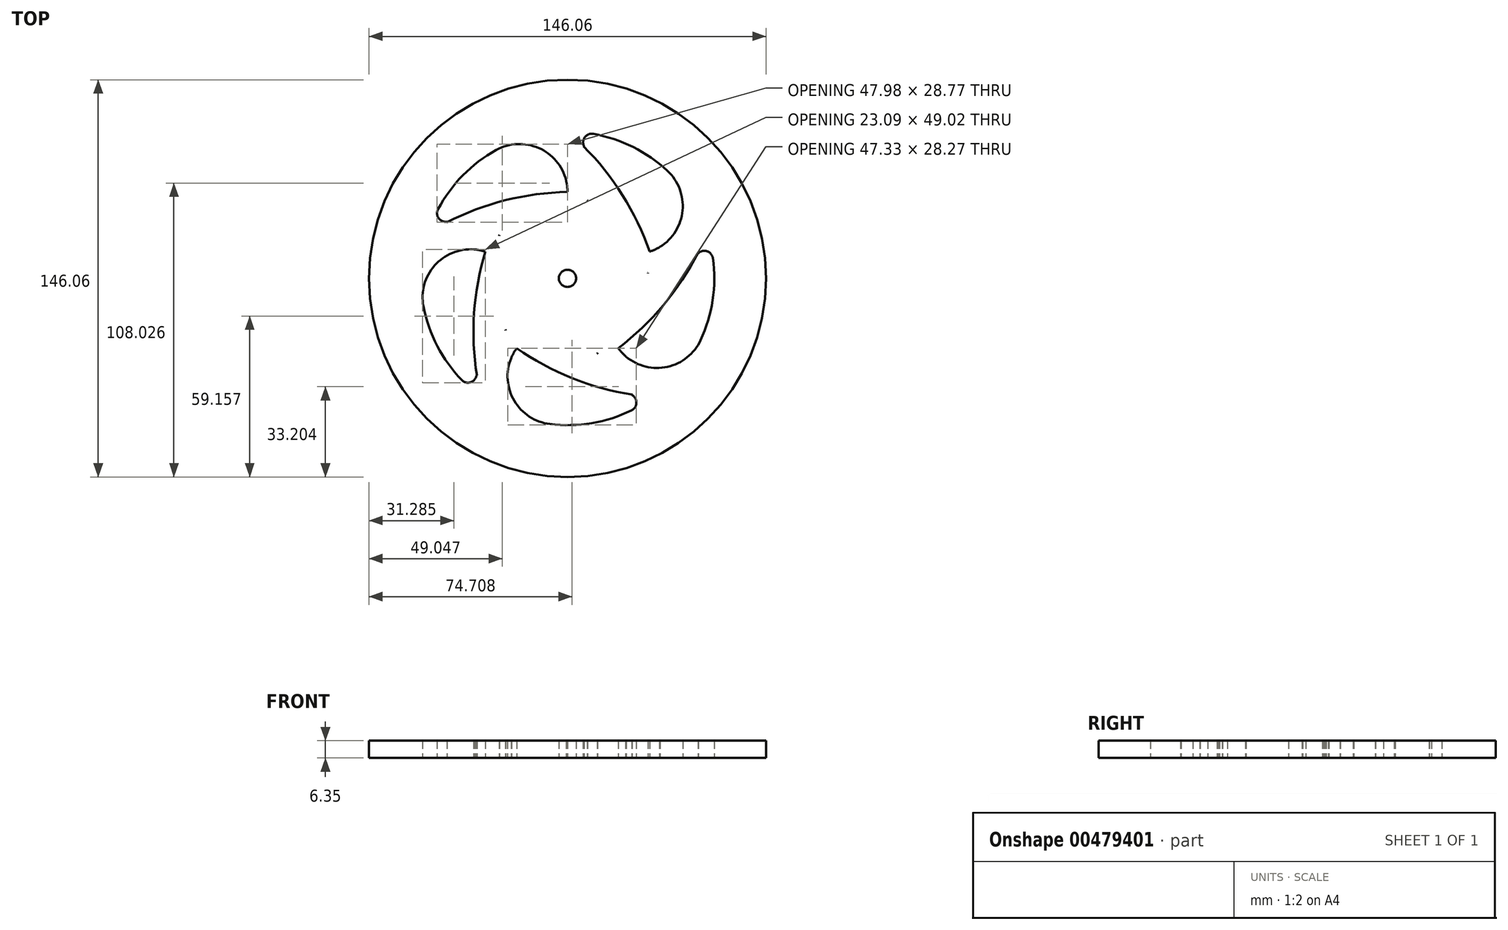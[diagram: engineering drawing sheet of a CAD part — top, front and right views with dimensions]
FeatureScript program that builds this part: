
annotation { "Feature Type Name" : "Feature", "Feature Type Description" : "" }
export const myFeature = defineFeature(function(context is Context, id is Id, definition is map)
    precondition{}
    {
        {
            var Q0;
            Q0=qCreatedBy(makeId("Top.planeOp"),FACE);
            var sketch = newSketch(context, id + "F0", { "sketchPlane" : qUnion([Q0]), "disableImprinting" : false});
            skCircle(sketch, "E0", {"center": v(0, 0) * mm, "radius": 73.03 * mm});
            skCircle(sketch, "E1", {"center": v(0, 0) * mm, "radius": 69.85 * mm});
            skLineSegment(sketch, "E2", {"start": v(-42.62, 55.34) * mm, "end": v(39.47, 57.63) * mm});
            skLineSegment(sketch, "E3", {"start": v(-42.62, 55.34) * mm, "end": v(-65.8, -23.44) * mm});
            skLineSegment(sketch, "E4", {"start": v(-65.8, -23.44) * mm, "end": v(1.96, -69.82) * mm});
            skLineSegment(sketch, "E5", {"start": v(1.96, -69.82) * mm, "end": v(67.01, -19.7) * mm});
            skLineSegment(sketch, "E6", {"start": v(67.01, -19.7) * mm, "end": v(39.47, 57.63) * mm});
            skCircle(sketch, "E7", {"center": v(1.96, -69.82) * mm, "radius": 101.6 * mm});
            skCircle(sketch, "E8", {"center": v(67.01, -19.7) * mm, "radius": 101.6 * mm});
            skCircle(sketch, "E9", {"center": v(39.47, 57.63) * mm, "radius": 101.6 * mm});
            skCircle(sketch, "E10", {"center": v(-42.62, 55.34) * mm, "radius": 101.6 * mm});
            skCircle(sketch, "E11", {"center": v(-65.8, -23.44) * mm, "radius": 101.6 * mm});
            skLineSegment(sketch, "E12", {"start": v(-232.09, 0) * mm, "end": v(227.68, 0) * mm});
            skCircle(sketch, "E13", {"center": v(0, 0) * mm, "radius": 53.97 * mm});
            skCircle(sketch, "E14.cCircle", {"center": v(0, 0) * mm, "radius": 36.32 * mm, "construction": true});
            skLineSegment(sketch, "E14.0", {"start": v(32.94, -15.31) * mm, "end": v(-4.38, -36.06) * mm});
            skLineSegment(sketch, "E14.1", {"start": v(-4.38, -36.06) * mm, "end": v(-35.65, -6.97) * mm});
            skLineSegment(sketch, "E14.2", {"start": v(-35.65, -6.97) * mm, "end": v(-17.65, 31.75) * mm});
            skLineSegment(sketch, "E14.3", {"start": v(-17.65, 31.75) * mm, "end": v(24.74, 26.6) * mm});
            skLineSegment(sketch, "E14.4", {"start": v(24.74, 26.6) * mm, "end": v(32.94, -15.31) * mm});
            skCircle(sketch, "E15", {"center": v(24.74, 26.6) * mm, "radius": 17.65 * mm});
            skCircle(sketch, "E16", {"center": v(-17.65, 31.75) * mm, "radius": 17.65 * mm});
            skCircle(sketch, "E17", {"center": v(-35.65, -6.97) * mm, "radius": 17.65 * mm});
            skCircle(sketch, "E18", {"center": v(-4.38, -36.06) * mm, "radius": 17.65 * mm});
            skCircle(sketch, "E19", {"center": v(32.94, -15.31) * mm, "radius": 17.65 * mm});
            skCircle(sketch, "E20.cCircle", {"center": v(0, 0) * mm, "radius": 50.8 * mm, "construction": true});
            skLineSegment(sketch, "E20.0", {"start": v(22.17, -45.7) * mm, "end": v(-36.62, -35.2) * mm});
            skLineSegment(sketch, "E20.1", {"start": v(-36.62, -35.2) * mm, "end": v(-44.8, 23.95) * mm});
            skLineSegment(sketch, "E20.2", {"start": v(-44.8, 23.95) * mm, "end": v(8.93, 50) * mm});
            skLineSegment(sketch, "E20.3", {"start": v(8.93, 50) * mm, "end": v(50.32, 6.96) * mm});
            skLineSegment(sketch, "E20.4", {"start": v(50.32, 6.96) * mm, "end": v(22.17, -45.7) * mm});
            skCircle(sketch, "E21", {"center": v(50.32, 6.96) * mm, "radius": 3.18 * mm});
            skCircle(sketch, "E22", {"center": v(8.93, 50) * mm, "radius": 3.18 * mm});
            skCircle(sketch, "E23", {"center": v(-44.8, 23.95) * mm, "radius": 3.18 * mm});
            skCircle(sketch, "E24", {"center": v(-36.62, -35.2) * mm, "radius": 3.18 * mm});
            skCircle(sketch, "E25", {"center": v(22.17, -45.7) * mm, "radius": 3.18 * mm});
            skCircle(sketch, "E26.cCircle", {"center": v(0, 0) * mm, "radius": 35.27 * mm, "construction": true});
            skLineSegment(sketch, "E26.0", {"start": v(23.5, -26.3) * mm, "end": v(-17.75, -30.48) * mm});
            skLineSegment(sketch, "E26.1", {"start": v(-17.75, -30.48) * mm, "end": v(-34.47, 7.46) * mm});
            skLineSegment(sketch, "E26.2", {"start": v(-34.47, 7.46) * mm, "end": v(-3.56, 35.09) * mm});
            skLineSegment(sketch, "E26.3", {"start": v(-3.56, 35.09) * mm, "end": v(32.27, 14.22) * mm});
            skLineSegment(sketch, "E26.4", {"start": v(32.27, 14.22) * mm, "end": v(23.5, -26.3) * mm});
            skCircle(sketch, "E27", {"center": v(32.27, 14.22) * mm, "radius": 3.18 * mm});
            skCircle(sketch, "E28", {"center": v(-3.56, 35.09) * mm, "radius": 3.18 * mm});
            skCircle(sketch, "E29", {"center": v(-34.47, 7.46) * mm, "radius": 3.18 * mm});
            skCircle(sketch, "E30", {"center": v(-17.75, -30.48) * mm, "radius": 3.18 * mm});
            skCircle(sketch, "E31", {"center": v(23.5, -26.3) * mm, "radius": 3.18 * mm});
            skCircle(sketch, "E32", {"center": v(0, 0) * mm, "radius": 3.18 * mm});
            skSolve(sketch);
        }
        {
            var Q0;
            {var subQ1=sQuery(id+"F0.wireOp",EDGE,"E0");var subQ6=sQuery(id+"F0.wireOp",EDGE,"E12");var subQ8=makeQuery(id+"F0.imprint","INTERSECT",VERTEX,{"disambiguationData":[OD(0.0)],"derivedFrom":[subQ1,subQ6]});Q0=makeQuery(id+"F0.imprint","IMPRINT",FACE,{"disambiguationData":[TD([[makeQuery(id+"F0.imprint","IMPRINT",EDGE,{"disambiguationData":[TD([[subQ8,1.0]])],"derivedFrom":subQ1}),1.0]])]});}
            var Q1;
            {var subQ0=sQuery(id+"F0.wireOp",EDGE,"E11");var subQ1=sQuery(id+"F0.wireOp",EDGE,"E0");var subQ2=makeQuery(id+"F0.imprint","INTERSECT",VERTEX,{"disambiguationData":[OD(1.0)],"derivedFrom":[subQ1,subQ0]});Q1=makeQuery(id+"F0.imprint","IMPRINT",FACE,{"disambiguationData":[TD([[makeQuery(id+"F0.imprint","IMPRINT",EDGE,{"disambiguationData":[TD([[subQ2,-1.0]])],"derivedFrom":subQ1}),1.0]])]});}
            var Q2;
            {var subQ0=sQuery(id+"F0.wireOp",EDGE,"E7");var subQ1=sQuery(id+"F0.wireOp",EDGE,"E0");var subQ2=makeQuery(id+"F0.imprint","INTERSECT",VERTEX,{"disambiguationData":[OD(0.0)],"derivedFrom":[subQ1,subQ0]});Q2=makeQuery(id+"F0.imprint","IMPRINT",FACE,{"disambiguationData":[TD([[makeQuery(id+"F0.imprint","IMPRINT",EDGE,{"disambiguationData":[TD([[subQ2,-1.0]])],"derivedFrom":subQ1}),1.0]])]});}
            var Q3;
            {var subQ0=sQuery(id+"F0.wireOp",EDGE,"E7");var subQ1=sQuery(id+"F0.wireOp",EDGE,"E0");var subQ2=makeQuery(id+"F0.imprint","INTERSECT",VERTEX,{"disambiguationData":[OD(0.0)],"derivedFrom":[subQ1,subQ0]});Q3=makeQuery(id+"F0.imprint","IMPRINT",FACE,{"disambiguationData":[TD([[makeQuery(id+"F0.imprint","IMPRINT",EDGE,{"disambiguationData":[TD([[subQ2,1.0]])],"derivedFrom":subQ1}),1.0]])]});}
            var Q4;
            {var subQ0=sQuery(id+"F0.wireOp",EDGE,"E8");var subQ1=sQuery(id+"F0.wireOp",EDGE,"E0");var subQ2=makeQuery(id+"F0.imprint","INTERSECT",VERTEX,{"disambiguationData":[OD(1.0)],"derivedFrom":[subQ1,subQ0]});Q4=makeQuery(id+"F0.imprint","IMPRINT",FACE,{"disambiguationData":[TD([[makeQuery(id+"F0.imprint","IMPRINT",EDGE,{"disambiguationData":[TD([[subQ2,-1.0]])],"derivedFrom":subQ1}),1.0]])]});}
            var Q5;
            {var subQ0=sQuery(id+"F0.wireOp",EDGE,"E10");var subQ1=sQuery(id+"F0.wireOp",EDGE,"E0");var subQ2=makeQuery(id+"F0.imprint","INTERSECT",VERTEX,{"disambiguationData":[OD(1.0)],"derivedFrom":[subQ1,subQ0]});Q5=makeQuery(id+"F0.imprint","IMPRINT",FACE,{"disambiguationData":[TD([[makeQuery(id+"F0.imprint","IMPRINT",EDGE,{"disambiguationData":[TD([[subQ2,-1.0]])],"derivedFrom":subQ1}),1.0]])]});}
            var Q6;
            {var subQ0=sQuery(id+"F0.wireOp",EDGE,"E7");var subQ1=sQuery(id+"F0.wireOp",EDGE,"E0");var subQ2=makeQuery(id+"F0.imprint","INTERSECT",VERTEX,{"disambiguationData":[OD(1.0)],"derivedFrom":[subQ1,subQ0]});Q6=makeQuery(id+"F0.imprint","IMPRINT",FACE,{"disambiguationData":[TD([[makeQuery(id+"F0.imprint","IMPRINT",EDGE,{"disambiguationData":[TD([[subQ2,-1.0]])],"derivedFrom":subQ1}),1.0]])]});}
            var Q7;
            {var subQ5=sQuery(id+"F0.wireOp",EDGE,"E9");var subQ6=sQuery(id+"F0.wireOp",EDGE,"E0");var subQ7=makeQuery(id+"F0.imprint","INTERSECT",VERTEX,{"disambiguationData":[OD(0.0)],"derivedFrom":[subQ6,subQ5]});Q7=makeQuery(id+"F0.imprint","IMPRINT",FACE,{"disambiguationData":[TD([[makeQuery(id+"F0.imprint","IMPRINT",EDGE,{"disambiguationData":[TD([[subQ7,-1.0]])],"derivedFrom":subQ6}),1.0]])]});}
            var Q8;
            {var subQ4=sQuery(id+"F0.wireOp",EDGE,"E11");var subQ6=sQuery(id+"F0.wireOp",EDGE,"E0");var subQ8=makeQuery(id+"F0.imprint","INTERSECT",VERTEX,{"disambiguationData":[OD(0.0)],"derivedFrom":[subQ6,subQ4]});Q8=makeQuery(id+"F0.imprint","IMPRINT",FACE,{"disambiguationData":[TD([[makeQuery(id+"F0.imprint","IMPRINT",EDGE,{"disambiguationData":[TD([[subQ8,-1.0]])],"derivedFrom":subQ6}),1.0]])]});}
            var Q9;
            {var subQ0=sQuery(id+"F0.wireOp",EDGE,"E8");var subQ1=sQuery(id+"F0.wireOp",EDGE,"E0");var subQ2=makeQuery(id+"F0.imprint","INTERSECT",VERTEX,{"disambiguationData":[OD(0.0)],"derivedFrom":[subQ1,subQ0]});Q9=makeQuery(id+"F0.imprint","IMPRINT",FACE,{"disambiguationData":[TD([[makeQuery(id+"F0.imprint","IMPRINT",EDGE,{"disambiguationData":[TD([[subQ2,-1.0]])],"derivedFrom":subQ1}),1.0]])]});}
            var Q10;
            {var subQ4=sQuery(id+"F0.wireOp",EDGE,"E10");var subQ6=sQuery(id+"F0.wireOp",EDGE,"E0");var subQ8=makeQuery(id+"F0.imprint","INTERSECT",VERTEX,{"disambiguationData":[OD(0.0)],"derivedFrom":[subQ6,subQ4]});Q10=makeQuery(id+"F0.imprint","IMPRINT",FACE,{"disambiguationData":[TD([[makeQuery(id+"F0.imprint","IMPRINT",EDGE,{"disambiguationData":[TD([[subQ8,-1.0]])],"derivedFrom":subQ6}),1.0]])]});}
            var Q11;
            {var subQ1=sQuery(id+"F0.wireOp",EDGE,"E1");var subQ3=sQuery(id+"F0.wireOp",EDGE,"E10");var subQ4=makeQuery(id+"F0.imprint","INTERSECT",VERTEX,{"disambiguationData":[OD(0.0)],"derivedFrom":[subQ1,subQ3]});Q11=makeQuery(id+"F0.imprint","IMPRINT",FACE,{"disambiguationData":[TD([[makeQuery(id+"F0.imprint","IMPRINT",EDGE,{"disambiguationData":[TD([[subQ4,1.0]])],"derivedFrom":subQ3}),1.0]])]});}
            var Q12;
            {var subQ0=sQuery(id+"F0.wireOp",EDGE,"E7");var subQ1=sQuery(id+"F0.wireOp",EDGE,"E1");var subQ2=makeQuery(id+"F0.imprint","INTERSECT",VERTEX,{"disambiguationData":[OD(0.0)],"derivedFrom":[subQ1,subQ0]});Q12=makeQuery(id+"F0.imprint","IMPRINT",FACE,{"disambiguationData":[TD([[makeQuery(id+"F0.imprint","IMPRINT",EDGE,{"disambiguationData":[TD([[subQ2,-1.0]])],"derivedFrom":subQ1}),1.0]])]});}
            var Q13;
            {var subQ0=sQuery(id+"F0.wireOp",EDGE,"E7");var subQ1=sQuery(id+"F0.wireOp",EDGE,"E1");var subQ2=makeQuery(id+"F0.imprint","INTERSECT",VERTEX,{"disambiguationData":[OD(0.0)],"derivedFrom":[subQ1,subQ0]});Q13=makeQuery(id+"F0.imprint","IMPRINT",FACE,{"disambiguationData":[TD([[makeQuery(id+"F0.imprint","IMPRINT",EDGE,{"disambiguationData":[TD([[subQ2,1.0]])],"derivedFrom":subQ1}),1.0]])]});}
            var Q14;
            {var subQ1=sQuery(id+"F0.wireOp",EDGE,"E1");var subQ3=sQuery(id+"F0.wireOp",EDGE,"E9");var subQ4=makeQuery(id+"F0.imprint","INTERSECT",VERTEX,{"disambiguationData":[OD(1.0)],"derivedFrom":[subQ1,subQ3]});Q14=makeQuery(id+"F0.imprint","IMPRINT",FACE,{"disambiguationData":[TD([[makeQuery(id+"F0.imprint","IMPRINT",EDGE,{"disambiguationData":[TD([[subQ4,1.0]])],"derivedFrom":subQ3}),1.0]])]});}
            var Q15;
            {var subQ0=sQuery(id+"F0.wireOp",EDGE,"E11");var subQ1=sQuery(id+"F0.wireOp",EDGE,"E1");var subQ2=makeQuery(id+"F0.imprint","INTERSECT",VERTEX,{"disambiguationData":[OD(1.0)],"derivedFrom":[subQ1,subQ0]});Q15=makeQuery(id+"F0.imprint","IMPRINT",FACE,{"disambiguationData":[TD([[makeQuery(id+"F0.imprint","IMPRINT",EDGE,{"disambiguationData":[TD([[subQ2,-1.0]])],"derivedFrom":subQ1}),1.0]])]});}
            var Q16;
            {var subQ1=sQuery(id+"F0.wireOp",EDGE,"E1");var subQ3=sQuery(id+"F0.wireOp",EDGE,"E11");var subQ4=makeQuery(id+"F0.imprint","INTERSECT",VERTEX,{"disambiguationData":[OD(1.0)],"derivedFrom":[subQ1,subQ3]});Q16=makeQuery(id+"F0.imprint","IMPRINT",FACE,{"disambiguationData":[TD([[makeQuery(id+"F0.imprint","IMPRINT",EDGE,{"disambiguationData":[TD([[subQ4,-1.0]])],"derivedFrom":subQ3}),1.0]])]});}
            var Q17;
            {var subQ0=sQuery(id+"F0.wireOp",EDGE,"E11");var subQ1=sQuery(id+"F0.wireOp",EDGE,"E5");var subQ2=makeQuery(id+"F0.imprint","INTERSECT",VERTEX,{"derivedFrom":[subQ1,subQ0]});Q17=makeQuery(id+"F0.imprint","IMPRINT",FACE,{"disambiguationData":[TD([[makeQuery(id+"F0.imprint","IMPRINT",EDGE,{"disambiguationData":[TD([[subQ2,-1.0]])],"derivedFrom":subQ1}),1.0]])]});}
            var Q18;
            {var subQ1=sQuery(id+"F0.wireOp",EDGE,"E1");var subQ3=sQuery(id+"F0.wireOp",EDGE,"E8");var subQ4=makeQuery(id+"F0.imprint","INTERSECT",VERTEX,{"disambiguationData":[OD(1.0)],"derivedFrom":[subQ1,subQ3]});Q18=makeQuery(id+"F0.imprint","IMPRINT",FACE,{"disambiguationData":[TD([[makeQuery(id+"F0.imprint","IMPRINT",EDGE,{"disambiguationData":[TD([[subQ4,1.0]])],"derivedFrom":subQ3}),1.0]])]});}
            var Q19;
            {var subQ0=sQuery(id+"F0.wireOp",EDGE,"E10");var subQ1=sQuery(id+"F0.wireOp",EDGE,"E1");var subQ2=makeQuery(id+"F0.imprint","INTERSECT",VERTEX,{"disambiguationData":[OD(1.0)],"derivedFrom":[subQ1,subQ0]});Q19=makeQuery(id+"F0.imprint","IMPRINT",FACE,{"disambiguationData":[TD([[makeQuery(id+"F0.imprint","IMPRINT",EDGE,{"disambiguationData":[TD([[subQ2,-1.0]])],"derivedFrom":subQ1}),1.0]])]});}
            var Q20;
            {var subQ1=sQuery(id+"F0.wireOp",EDGE,"E1");var subQ3=sQuery(id+"F0.wireOp",EDGE,"E12");var subQ4=makeQuery(id+"F0.imprint","INTERSECT",VERTEX,{"disambiguationData":[OD(1.0)],"derivedFrom":[subQ1,subQ3]});Q20=makeQuery(id+"F0.imprint","IMPRINT",FACE,{"disambiguationData":[TD([[makeQuery(id+"F0.imprint","IMPRINT",EDGE,{"disambiguationData":[TD([[subQ4,-1.0]])],"derivedFrom":subQ3}),-1.0]])]});}
            var Q21;
            {var subQ0=sQuery(id+"F0.wireOp",EDGE,"E7");var subQ1=sQuery(id+"F0.wireOp",EDGE,"E1");var subQ2=makeQuery(id+"F0.imprint","INTERSECT",VERTEX,{"disambiguationData":[OD(1.0)],"derivedFrom":[subQ1,subQ0]});Q21=makeQuery(id+"F0.imprint","IMPRINT",FACE,{"disambiguationData":[TD([[makeQuery(id+"F0.imprint","IMPRINT",EDGE,{"disambiguationData":[TD([[subQ2,-1.0]])],"derivedFrom":subQ1}),-1.0]])]});}
            var Q22;
            {var subQ0=sQuery(id+"F0.wireOp",EDGE,"E12");var subQ1=sQuery(id+"F0.wireOp",EDGE,"E0");var subQ2=makeQuery(id+"F0.imprint","INTERSECT",VERTEX,{"disambiguationData":[OD(1.0)],"derivedFrom":[subQ1,subQ0]});Q22=makeQuery(id+"F0.imprint","IMPRINT",FACE,{"disambiguationData":[TD([[makeQuery(id+"F0.imprint","IMPRINT",EDGE,{"disambiguationData":[TD([[subQ2,-1.0]])],"derivedFrom":subQ1}),1.0]])]});}
            var Q23;
            {var subQ0=sQuery(id+"F0.wireOp",EDGE,"E9");var subQ1=sQuery(id+"F0.wireOp",EDGE,"E1");var subQ2=makeQuery(id+"F0.imprint","INTERSECT",VERTEX,{"disambiguationData":[OD(0.0)],"derivedFrom":[subQ1,subQ0]});Q23=makeQuery(id+"F0.imprint","IMPRINT",FACE,{"disambiguationData":[TD([[makeQuery(id+"F0.imprint","IMPRINT",EDGE,{"disambiguationData":[TD([[subQ2,-1.0]])],"derivedFrom":subQ1}),1.0]])]});}
            var Q24;
            {var subQ1=sQuery(id+"F0.wireOp",EDGE,"E1");var subQ3=sQuery(id+"F0.wireOp",EDGE,"E9");var subQ4=makeQuery(id+"F0.imprint","INTERSECT",VERTEX,{"disambiguationData":[OD(0.0)],"derivedFrom":[subQ1,subQ3]});Q24=makeQuery(id+"F0.imprint","IMPRINT",FACE,{"disambiguationData":[TD([[makeQuery(id+"F0.imprint","IMPRINT",EDGE,{"disambiguationData":[TD([[subQ4,-1.0]])],"derivedFrom":subQ3}),1.0]])]});}
            var Q25;
            {var subQ1=sQuery(id+"F0.wireOp",EDGE,"E1");var subQ3=sQuery(id+"F0.wireOp",EDGE,"E11");var subQ4=makeQuery(id+"F0.imprint","INTERSECT",VERTEX,{"disambiguationData":[OD(0.0)],"derivedFrom":[subQ1,subQ3]});Q25=makeQuery(id+"F0.imprint","IMPRINT",FACE,{"disambiguationData":[TD([[makeQuery(id+"F0.imprint","IMPRINT",EDGE,{"disambiguationData":[TD([[subQ4,1.0]])],"derivedFrom":subQ3}),1.0]])]});}
            var Q26;
            {var subQ1=sQuery(id+"F0.wireOp",EDGE,"E1");var subQ3=sQuery(id+"F0.wireOp",EDGE,"E8");var subQ4=makeQuery(id+"F0.imprint","INTERSECT",VERTEX,{"disambiguationData":[OD(0.0)],"derivedFrom":[subQ1,subQ3]});Q26=makeQuery(id+"F0.imprint","IMPRINT",FACE,{"disambiguationData":[TD([[makeQuery(id+"F0.imprint","IMPRINT",EDGE,{"disambiguationData":[TD([[subQ4,-1.0]])],"derivedFrom":subQ3}),1.0]])]});}
            var Q27;
            {var subQ0=sQuery(id+"F0.wireOp",EDGE,"E8");var subQ1=sQuery(id+"F0.wireOp",EDGE,"E1");var subQ2=makeQuery(id+"F0.imprint","INTERSECT",VERTEX,{"disambiguationData":[OD(0.0)],"derivedFrom":[subQ1,subQ0]});Q27=makeQuery(id+"F0.imprint","IMPRINT",FACE,{"disambiguationData":[TD([[makeQuery(id+"F0.imprint","IMPRINT",EDGE,{"disambiguationData":[TD([[subQ2,-1.0]])],"derivedFrom":subQ1}),1.0]])]});}
            var Q28;
            {var subQ3=sQuery(id+"F0.wireOp",EDGE,"E13");var subQ5=sQuery(id+"F0.wireOp",EDGE,"E7");var subQ6=makeQuery(id+"F0.imprint","INTERSECT",VERTEX,{"disambiguationData":[OD(1.0)],"derivedFrom":[subQ5,subQ3]});Q28=makeQuery(id+"F0.imprint","IMPRINT",FACE,{"disambiguationData":[TD([[makeQuery(id+"F0.imprint","IMPRINT",EDGE,{"disambiguationData":[TD([[subQ6,-1.0]])],"derivedFrom":subQ5}),-1.0]])]});}
            var Q29;
            {var subQ0=sQuery(id+"F0.wireOp",EDGE,"E11");var subQ1=sQuery(id+"F0.wireOp",EDGE,"E2");var subQ2=makeQuery(id+"F0.imprint","INTERSECT",VERTEX,{"derivedFrom":[subQ1,subQ0]});Q29=makeQuery(id+"F0.imprint","IMPRINT",FACE,{"disambiguationData":[TD([[makeQuery(id+"F0.imprint","IMPRINT",EDGE,{"disambiguationData":[TD([[subQ2,-1.0]])],"derivedFrom":subQ1}),-1.0]])]});}
            var Q30;
            {var subQ0=sQuery(id+"F0.wireOp",EDGE,"E11");var subQ1=sQuery(id+"F0.wireOp",EDGE,"E8");var subQ2=makeQuery(id+"F0.imprint","INTERSECT",VERTEX,{"disambiguationData":[OD(0.0)],"derivedFrom":[subQ1,subQ0]});Q30=makeQuery(id+"F0.imprint","IMPRINT",FACE,{"disambiguationData":[TD([[makeQuery(id+"F0.imprint","IMPRINT",EDGE,{"disambiguationData":[TD([[subQ2,-1.0]])],"derivedFrom":subQ1}),1.0]])]});}
            var Q31;
            {var subQ1=sQuery(id+"F0.wireOp",EDGE,"E8");var subQ5=sQuery(id+"F0.wireOp",EDGE,"E13");var subQ6=makeQuery(id+"F0.imprint","INTERSECT",VERTEX,{"disambiguationData":[OD(0.0)],"derivedFrom":[subQ1,subQ5]});Q31=makeQuery(id+"F0.imprint","IMPRINT",FACE,{"disambiguationData":[TD([[makeQuery(id+"F0.imprint","IMPRINT",EDGE,{"disambiguationData":[TD([[subQ6,-1.0]])],"derivedFrom":subQ1}),1.0]])]});}
            var Q32;
            {var subQ0=sQuery(id+"F0.wireOp",EDGE,"E13");var subQ1=sQuery(id+"F0.wireOp",EDGE,"E8");var subQ2=makeQuery(id+"F0.imprint","INTERSECT",VERTEX,{"disambiguationData":[OD(0.0)],"derivedFrom":[subQ1,subQ0]});Q32=makeQuery(id+"F0.imprint","IMPRINT",FACE,{"disambiguationData":[TD([[makeQuery(id+"F0.imprint","IMPRINT",EDGE,{"disambiguationData":[TD([[subQ2,-1.0]])],"derivedFrom":subQ1}),-1.0]])]});}
            var Q33;
            {var subQ0=sQuery(id+"F0.wireOp",EDGE,"E20.2");var subQ1=sQuery(id+"F0.wireOp",EDGE,"E11");var subQ2=makeQuery(id+"F0.imprint","INTERSECT",VERTEX,{"derivedFrom":[subQ1,subQ0]});Q33=makeQuery(id+"F0.imprint","IMPRINT",FACE,{"disambiguationData":[TD([[makeQuery(id+"F0.imprint","IMPRINT",EDGE,{"disambiguationData":[TD([[subQ2,-1.0]])],"derivedFrom":subQ1}),-1.0]])]});}
            var Q34;
            {var subQ0=sQuery(id+"F0.wireOp",EDGE,"E9");var subQ1=sQuery(id+"F0.wireOp",EDGE,"E3");var subQ2=makeQuery(id+"F0.imprint","INTERSECT",VERTEX,{"derivedFrom":[subQ1,subQ0]});Q34=makeQuery(id+"F0.imprint","IMPRINT",FACE,{"disambiguationData":[TD([[makeQuery(id+"F0.imprint","IMPRINT",EDGE,{"disambiguationData":[TD([[subQ2,-1.0]])],"derivedFrom":subQ1}),1.0]])]});}
            var Q35;
            {var subQ0=sQuery(id+"F0.wireOp",EDGE,"E13");var subQ1=sQuery(id+"F0.wireOp",EDGE,"E7");var subQ2=makeQuery(id+"F0.imprint","INTERSECT",VERTEX,{"disambiguationData":[OD(1.0)],"derivedFrom":[subQ1,subQ0]});Q35=makeQuery(id+"F0.imprint","IMPRINT",FACE,{"disambiguationData":[TD([[makeQuery(id+"F0.imprint","IMPRINT",EDGE,{"disambiguationData":[TD([[subQ2,-1.0]])],"derivedFrom":subQ1}),1.0]])]});}
            var Q36;
            {var subQ0=sQuery(id+"F0.wireOp",EDGE,"E7");var subQ1=sQuery(id+"F0.wireOp",EDGE,"E1");var subQ2=makeQuery(id+"F0.imprint","INTERSECT",VERTEX,{"disambiguationData":[OD(1.0)],"derivedFrom":[subQ1,subQ0]});Q36=makeQuery(id+"F0.imprint","IMPRINT",FACE,{"disambiguationData":[TD([[makeQuery(id+"F0.imprint","IMPRINT",EDGE,{"disambiguationData":[TD([[subQ2,-1.0]])],"derivedFrom":subQ1}),1.0]])]});}
            var Q37;
            {var subQ1=sQuery(id+"F0.wireOp",EDGE,"E7");var subQ6=sQuery(id+"F0.wireOp",EDGE,"E3");var subQ9=makeQuery(id+"F0.imprint","INTERSECT",VERTEX,{"derivedFrom":[subQ6,subQ1]});Q37=makeQuery(id+"F0.imprint","IMPRINT",FACE,{"disambiguationData":[TD([[makeQuery(id+"F0.imprint","IMPRINT",EDGE,{"disambiguationData":[TD([[subQ9,-1.0]])],"derivedFrom":subQ6}),1.0]])]});}
            var Q38;
            {var subQ3=sQuery(id+"F0.wireOp",EDGE,"E8");var subQ5=sQuery(id+"F0.wireOp",EDGE,"E13");var subQ11=makeQuery(id+"F0.imprint","INTERSECT",VERTEX,{"disambiguationData":[OD(1.0)],"derivedFrom":[subQ3,subQ5]});Q38=makeQuery(id+"F0.imprint","IMPRINT",FACE,{"disambiguationData":[TD([[makeQuery(id+"F0.imprint","IMPRINT",EDGE,{"disambiguationData":[TD([[subQ11,-1.0]])],"derivedFrom":subQ3}),-1.0]])]});}
            var Q39;
            {var subQ1=sQuery(id+"F0.wireOp",EDGE,"E1");var subQ3=sQuery(id+"F0.wireOp",EDGE,"E12");var subQ4=makeQuery(id+"F0.imprint","INTERSECT",VERTEX,{"disambiguationData":[OD(0.0)],"derivedFrom":[subQ1,subQ3]});Q39=makeQuery(id+"F0.imprint","IMPRINT",FACE,{"disambiguationData":[TD([[makeQuery(id+"F0.imprint","IMPRINT",EDGE,{"disambiguationData":[TD([[subQ4,1.0]])],"derivedFrom":subQ3}),-1.0]])]});}
            var Q40;
            {var subQ1=sQuery(id+"F0.wireOp",EDGE,"E9");var subQ5=sQuery(id+"F0.wireOp",EDGE,"E5");var subQ6=makeQuery(id+"F0.imprint","INTERSECT",VERTEX,{"derivedFrom":[subQ5,subQ1]});Q40=makeQuery(id+"F0.imprint","IMPRINT",FACE,{"disambiguationData":[TD([[makeQuery(id+"F0.imprint","IMPRINT",EDGE,{"disambiguationData":[TD([[subQ6,1.0]])],"derivedFrom":subQ1}),1.0]])]});}
            var Q41;
            {var subQ0=sQuery(id+"F0.wireOp",EDGE,"E12");var subQ1=sQuery(id+"F0.wireOp",EDGE,"E6");var subQ2=makeQuery(id+"F0.imprint","INTERSECT",VERTEX,{"derivedFrom":[subQ1,subQ0]});Q41=makeQuery(id+"F0.imprint","IMPRINT",FACE,{"disambiguationData":[TD([[makeQuery(id+"F0.imprint","IMPRINT",EDGE,{"disambiguationData":[TD([[subQ2,-1.0]])],"derivedFrom":subQ1}),1.0]])]});}
            var Q42;
            {var subQ1=sQuery(id+"F0.wireOp",EDGE,"E1");var subQ3=sQuery(id+"F0.wireOp",EDGE,"E10");var subQ4=makeQuery(id+"F0.imprint","INTERSECT",VERTEX,{"disambiguationData":[OD(1.0)],"derivedFrom":[subQ1,subQ3]});Q42=makeQuery(id+"F0.imprint","IMPRINT",FACE,{"disambiguationData":[TD([[makeQuery(id+"F0.imprint","IMPRINT",EDGE,{"disambiguationData":[TD([[subQ4,-1.0]])],"derivedFrom":subQ3}),1.0]])]});}
            var Q43;
            {var subQ9=sQuery(id+"F0.wireOp",EDGE,"E17");var subQ13=sQuery(id+"F0.wireOp",EDGE,"E12");var subQ14=makeQuery(id+"F0.imprint","INTERSECT",VERTEX,{"disambiguationData":[OD(1.0)],"derivedFrom":[subQ13,subQ9]});Q43=makeQuery(id+"F0.imprint","IMPRINT",FACE,{"disambiguationData":[TD([[makeQuery(id+"F0.imprint","IMPRINT",EDGE,{"disambiguationData":[TD([[subQ14,-1.0]])],"derivedFrom":subQ13}),1.0]])]});}
            var Q44;
            {var subQ0=sQuery(id+"F0.wireOp",EDGE,"E17");var subQ1=sQuery(id+"F0.wireOp",EDGE,"E12");var subQ2=makeQuery(id+"F0.imprint","INTERSECT",VERTEX,{"disambiguationData":[OD(1.0)],"derivedFrom":[subQ1,subQ0]});Q44=makeQuery(id+"F0.imprint","IMPRINT",FACE,{"disambiguationData":[TD([[makeQuery(id+"F0.imprint","IMPRINT",EDGE,{"disambiguationData":[TD([[subQ2,-1.0]])],"derivedFrom":subQ1}),-1.0]])]});}
            var Q45;
            {var subQ7=sQuery(id+"F0.wireOp",EDGE,"E10");var subQ9=sQuery(id+"F0.wireOp",EDGE,"E7");var subQ10=makeQuery(id+"F0.imprint","INTERSECT",VERTEX,{"disambiguationData":[OD(0.0)],"derivedFrom":[subQ9,subQ7]});Q45=makeQuery(id+"F0.imprint","IMPRINT",FACE,{"disambiguationData":[TD([[makeQuery(id+"F0.imprint","IMPRINT",EDGE,{"disambiguationData":[TD([[subQ10,-1.0]])],"derivedFrom":subQ9}),-1.0]])]});}
            var Q46;
            {var subQ0=sQuery(id+"F0.wireOp",EDGE,"E15");var subQ1=sQuery(id+"F0.wireOp",EDGE,"E14.3");var subQ2=makeQuery(id+"F0.imprint","INTERSECT",VERTEX,{"derivedFrom":[subQ1,subQ0]});Q46=makeQuery(id+"F0.imprint","IMPRINT",FACE,{"disambiguationData":[TD([[makeQuery(id+"F0.imprint","IMPRINT",EDGE,{"disambiguationData":[TD([[subQ2,-1.0]])],"derivedFrom":subQ1}),-1.0]])]});}
            var Q47;
            {var subQ0=sQuery(id+"F0.wireOp",EDGE,"E16");var subQ1=sQuery(id+"F0.wireOp",EDGE,"E14.2");var subQ2=makeQuery(id+"F0.imprint","INTERSECT",VERTEX,{"derivedFrom":[subQ1,subQ0]});Q47=makeQuery(id+"F0.imprint","IMPRINT",FACE,{"disambiguationData":[TD([[makeQuery(id+"F0.imprint","IMPRINT",EDGE,{"disambiguationData":[TD([[subQ2,-1.0]])],"derivedFrom":subQ1}),-1.0]])]});}
            var Q48;
            {var subQ0=sQuery(id+"F0.wireOp",EDGE,"E26.1");var subQ1=sQuery(id+"F0.wireOp",EDGE,"E12");var subQ2=makeQuery(id+"F0.imprint","INTERSECT",VERTEX,{"derivedFrom":[subQ1,subQ0]});Q48=makeQuery(id+"F0.imprint","IMPRINT",FACE,{"disambiguationData":[TD([[makeQuery(id+"F0.imprint","IMPRINT",EDGE,{"disambiguationData":[TD([[subQ2,-1.0]])],"derivedFrom":subQ1}),-1.0]])]});}
            var Q49;
            {var subQ0=sQuery(id+"F0.wireOp",EDGE,"E26.1");var subQ1=sQuery(id+"F0.wireOp",EDGE,"E12");var subQ2=makeQuery(id+"F0.imprint","INTERSECT",VERTEX,{"derivedFrom":[subQ1,subQ0]});Q49=makeQuery(id+"F0.imprint","IMPRINT",FACE,{"disambiguationData":[TD([[makeQuery(id+"F0.imprint","IMPRINT",EDGE,{"disambiguationData":[TD([[subQ2,-1.0]])],"derivedFrom":subQ1}),1.0]])]});}
            var Q50;
            {var subQ0=sQuery(id+"F0.wireOp",EDGE,"E18");var subQ1=sQuery(id+"F0.wireOp",EDGE,"E14.0");var subQ2=makeQuery(id+"F0.imprint","INTERSECT",VERTEX,{"derivedFrom":[subQ1,subQ0]});Q50=makeQuery(id+"F0.imprint","IMPRINT",FACE,{"disambiguationData":[TD([[makeQuery(id+"F0.imprint","IMPRINT",EDGE,{"disambiguationData":[TD([[subQ2,-1.0]])],"derivedFrom":subQ1}),-1.0]])]});}
            var Q51;
            {var subQ0=sQuery(id+"F0.wireOp",EDGE,"E19");var subQ1=sQuery(id+"F0.wireOp",EDGE,"E12");var subQ2=makeQuery(id+"F0.imprint","INTERSECT",VERTEX,{"disambiguationData":[OD(0.0)],"derivedFrom":[subQ1,subQ0]});Q51=makeQuery(id+"F0.imprint","IMPRINT",FACE,{"disambiguationData":[TD([[makeQuery(id+"F0.imprint","IMPRINT",EDGE,{"disambiguationData":[TD([[subQ2,-1.0]])],"derivedFrom":subQ1}),-1.0]])]});}
            var Q52;
            {var subQ5=sQuery(id+"F0.wireOp",EDGE,"E16");var subQ9=sQuery(id+"F0.wireOp",EDGE,"E7");var subQ10=makeQuery(id+"F0.imprint","INTERSECT",VERTEX,{"disambiguationData":[OD(1.0)],"derivedFrom":[subQ9,subQ5]});Q52=makeQuery(id+"F0.imprint","IMPRINT",FACE,{"disambiguationData":[TD([[makeQuery(id+"F0.imprint","IMPRINT",EDGE,{"disambiguationData":[TD([[subQ10,-1.0]])],"derivedFrom":subQ9}),1.0]])]});}
            var Q53;
            {var subQ0=sQuery(id+"F0.wireOp",EDGE,"E20.1");var subQ1=sQuery(id+"F0.wireOp",EDGE,"E7");var subQ2=makeQuery(id+"F0.imprint","INTERSECT",VERTEX,{"derivedFrom":[subQ1,subQ0]});Q53=makeQuery(id+"F0.imprint","IMPRINT",FACE,{"disambiguationData":[TD([[makeQuery(id+"F0.imprint","IMPRINT",EDGE,{"disambiguationData":[TD([[subQ2,-1.0]])],"derivedFrom":subQ1}),-1.0]])]});}
            var Q54;
            {var subQ0=sQuery(id+"F0.wireOp",EDGE,"E13");var subQ1=sQuery(id+"F0.wireOp",EDGE,"E9");var subQ2=makeQuery(id+"F0.imprint","INTERSECT",VERTEX,{"disambiguationData":[OD(0.0)],"derivedFrom":[subQ1,subQ0]});Q54=makeQuery(id+"F0.imprint","IMPRINT",FACE,{"disambiguationData":[TD([[makeQuery(id+"F0.imprint","IMPRINT",EDGE,{"disambiguationData":[TD([[subQ2,-1.0]])],"derivedFrom":subQ1}),-1.0]])]});}
            var Q55;
            {var subQ0=sQuery(id+"F0.wireOp",EDGE,"E15");var subQ1=sQuery(id+"F0.wireOp",EDGE,"E7");var subQ2=makeQuery(id+"F0.imprint","INTERSECT",VERTEX,{"disambiguationData":[OD(1.0)],"derivedFrom":[subQ1,subQ0]});Q55=makeQuery(id+"F0.imprint","IMPRINT",FACE,{"disambiguationData":[TD([[makeQuery(id+"F0.imprint","IMPRINT",EDGE,{"disambiguationData":[TD([[subQ2,-1.0]])],"derivedFrom":subQ1}),-1.0]])]});}
            var Q56;
            {var subQ3=sQuery(id+"F0.wireOp",EDGE,"E26.3");var subQ7=sQuery(id+"F0.wireOp",EDGE,"E7");var subQ9=makeQuery(id+"F0.imprint","INTERSECT",VERTEX,{"derivedFrom":[subQ7,subQ3]});Q56=makeQuery(id+"F0.imprint","IMPRINT",FACE,{"disambiguationData":[TD([[makeQuery(id+"F0.imprint","IMPRINT",EDGE,{"disambiguationData":[TD([[subQ9,-1.0]])],"derivedFrom":subQ7}),1.0]])]});}
            var Q57;
            {var subQ0=sQuery(id+"F0.wireOp",EDGE,"E15");var subQ1=sQuery(id+"F0.wireOp",EDGE,"E7");var subQ2=makeQuery(id+"F0.imprint","INTERSECT",VERTEX,{"disambiguationData":[OD(1.0)],"derivedFrom":[subQ1,subQ0]});Q57=makeQuery(id+"F0.imprint","IMPRINT",FACE,{"disambiguationData":[TD([[makeQuery(id+"F0.imprint","IMPRINT",EDGE,{"disambiguationData":[TD([[subQ2,-1.0]])],"derivedFrom":subQ1}),1.0]])]});}
            var Q58;
            {var subQ0=sQuery(id+"F0.wireOp",EDGE,"E26.3");var subQ1=sQuery(id+"F0.wireOp",EDGE,"E7");var subQ2=makeQuery(id+"F0.imprint","INTERSECT",VERTEX,{"derivedFrom":[subQ1,subQ0]});Q58=makeQuery(id+"F0.imprint","IMPRINT",FACE,{"disambiguationData":[TD([[makeQuery(id+"F0.imprint","IMPRINT",EDGE,{"disambiguationData":[TD([[subQ2,-1.0]])],"derivedFrom":subQ1}),-1.0]])]});}
            var Q59;
            {var subQ0=sQuery(id+"F0.wireOp",EDGE,"E8");var subQ1=sQuery(id+"F0.wireOp",EDGE,"E7");var subQ2=makeQuery(id+"F0.imprint","INTERSECT",VERTEX,{"disambiguationData":[OD(1.0)],"derivedFrom":[subQ1,subQ0]});Q59=makeQuery(id+"F0.imprint","IMPRINT",FACE,{"disambiguationData":[TD([[makeQuery(id+"F0.imprint","IMPRINT",EDGE,{"disambiguationData":[TD([[subQ2,-1.0]])],"derivedFrom":subQ1}),1.0]])]});}
            var Q60;
            {var subQ0=sQuery(id+"F0.wireOp",EDGE,"E14.2");var subQ1=sQuery(id+"F0.wireOp",EDGE,"E7");var subQ2=makeQuery(id+"F0.imprint","INTERSECT",VERTEX,{"derivedFrom":[subQ1,subQ0]});Q60=makeQuery(id+"F0.imprint","IMPRINT",FACE,{"disambiguationData":[TD([[makeQuery(id+"F0.imprint","IMPRINT",EDGE,{"disambiguationData":[TD([[subQ2,-1.0]])],"derivedFrom":subQ1}),1.0]])]});}
            var Q61;
            {var subQ0=sQuery(id+"F0.wireOp",EDGE,"E14.3");var subQ1=sQuery(id+"F0.wireOp",EDGE,"E7");var subQ2=makeQuery(id+"F0.imprint","INTERSECT",VERTEX,{"derivedFrom":[subQ1,subQ0]});Q61=makeQuery(id+"F0.imprint","IMPRINT",FACE,{"disambiguationData":[TD([[makeQuery(id+"F0.imprint","IMPRINT",EDGE,{"disambiguationData":[TD([[subQ2,-1.0]])],"derivedFrom":subQ1}),1.0]])]});}
            var Q62;
            {var subQ0=sQuery(id+"F0.wireOp",EDGE,"E16");var subQ1=sQuery(id+"F0.wireOp",EDGE,"E7");var subQ2=makeQuery(id+"F0.imprint","INTERSECT",VERTEX,{"disambiguationData":[OD(0.0)],"derivedFrom":[subQ1,subQ0]});Q62=makeQuery(id+"F0.imprint","IMPRINT",FACE,{"disambiguationData":[TD([[makeQuery(id+"F0.imprint","IMPRINT",EDGE,{"disambiguationData":[TD([[subQ2,-1.0]])],"derivedFrom":subQ1}),1.0]])]});}
            var Q63;
            {var subQ0=sQuery(id+"F0.wireOp",EDGE,"E26.2");var subQ1=sQuery(id+"F0.wireOp",EDGE,"E7");var subQ2=makeQuery(id+"F0.imprint","INTERSECT",VERTEX,{"derivedFrom":[subQ1,subQ0]});Q63=makeQuery(id+"F0.imprint","IMPRINT",FACE,{"disambiguationData":[TD([[makeQuery(id+"F0.imprint","IMPRINT",EDGE,{"disambiguationData":[TD([[subQ2,-1.0]])],"derivedFrom":subQ1}),1.0]])]});}
            var Q64;
            {var subQ0=sQuery(id+"F0.wireOp",EDGE,"E11");var subQ1=sQuery(id+"F0.wireOp",EDGE,"E7");var subQ2=makeQuery(id+"F0.imprint","INTERSECT",VERTEX,{"disambiguationData":[OD(1.0)],"derivedFrom":[subQ1,subQ0]});Q64=makeQuery(id+"F0.imprint","IMPRINT",FACE,{"disambiguationData":[TD([[makeQuery(id+"F0.imprint","IMPRINT",EDGE,{"disambiguationData":[TD([[subQ2,-1.0]])],"derivedFrom":subQ1}),-1.0]])]});}
            var Q65;
            {var subQ1=sQuery(id+"F0.wireOp",EDGE,"E11");var subQ5=sQuery(id+"F0.wireOp",EDGE,"E7");var subQ6=makeQuery(id+"F0.imprint","INTERSECT",VERTEX,{"disambiguationData":[OD(1.0)],"derivedFrom":[subQ5,subQ1]});Q65=makeQuery(id+"F0.imprint","IMPRINT",FACE,{"disambiguationData":[TD([[makeQuery(id+"F0.imprint","IMPRINT",EDGE,{"disambiguationData":[TD([[subQ6,-1.0]])],"derivedFrom":subQ5}),1.0]])]});}
            var Q66;
            {var subQ0=sQuery(id+"F0.wireOp",EDGE,"E14.4");var subQ1=sQuery(id+"F0.wireOp",EDGE,"E11");var subQ2=makeQuery(id+"F0.imprint","INTERSECT",VERTEX,{"derivedFrom":[subQ1,subQ0]});Q66=makeQuery(id+"F0.imprint","IMPRINT",FACE,{"disambiguationData":[TD([[makeQuery(id+"F0.imprint","IMPRINT",EDGE,{"disambiguationData":[TD([[subQ2,-1.0]])],"derivedFrom":subQ1}),1.0]])]});}
            var Q67;
            {var subQ0=sQuery(id+"F0.wireOp",EDGE,"E15");var subQ1=sQuery(id+"F0.wireOp",EDGE,"E11");var subQ2=makeQuery(id+"F0.imprint","INTERSECT",VERTEX,{"disambiguationData":[OD(0.0)],"derivedFrom":[subQ1,subQ0]});Q67=makeQuery(id+"F0.imprint","IMPRINT",FACE,{"disambiguationData":[TD([[makeQuery(id+"F0.imprint","IMPRINT",EDGE,{"disambiguationData":[TD([[subQ2,-1.0]])],"derivedFrom":subQ1}),1.0]])]});}
            var Q68;
            {var subQ5=sQuery(id+"F0.wireOp",EDGE,"E12");var subQ6=sQuery(id+"F0.wireOp",EDGE,"E10");var subQ7=makeQuery(id+"F0.imprint","INTERSECT",VERTEX,{"disambiguationData":[OD(1.0)],"derivedFrom":[subQ6,subQ5]});Q68=makeQuery(id+"F0.imprint","IMPRINT",FACE,{"disambiguationData":[TD([[makeQuery(id+"F0.imprint","IMPRINT",EDGE,{"disambiguationData":[TD([[subQ7,-1.0]])],"derivedFrom":subQ6}),1.0]])]});}
            var Q69;
            {var subQ1=sQuery(id+"F0.wireOp",EDGE,"E7");var subQ5=sQuery(id+"F0.wireOp",EDGE,"E13");var subQ6=makeQuery(id+"F0.imprint","INTERSECT",VERTEX,{"disambiguationData":[OD(0.0)],"derivedFrom":[subQ1,subQ5]});Q69=makeQuery(id+"F0.imprint","IMPRINT",FACE,{"disambiguationData":[TD([[makeQuery(id+"F0.imprint","IMPRINT",EDGE,{"disambiguationData":[TD([[subQ6,-1.0]])],"derivedFrom":subQ1}),1.0]])]});}
            var Q70;
            {var subQ0=sQuery(id+"F0.wireOp",EDGE,"E13");var subQ1=sQuery(id+"F0.wireOp",EDGE,"E7");var subQ2=makeQuery(id+"F0.imprint","INTERSECT",VERTEX,{"disambiguationData":[OD(0.0)],"derivedFrom":[subQ1,subQ0]});Q70=makeQuery(id+"F0.imprint","IMPRINT",FACE,{"disambiguationData":[TD([[makeQuery(id+"F0.imprint","IMPRINT",EDGE,{"disambiguationData":[TD([[subQ2,-1.0]])],"derivedFrom":subQ1}),-1.0]])]});}
            var Q71;
            {var subQ0=sQuery(id+"F0.wireOp",EDGE,"E19");var subQ1=sQuery(id+"F0.wireOp",EDGE,"E12");var subQ2=makeQuery(id+"F0.imprint","INTERSECT",VERTEX,{"disambiguationData":[OD(0.0)],"derivedFrom":[subQ1,subQ0]});Q71=makeQuery(id+"F0.imprint","IMPRINT",FACE,{"disambiguationData":[TD([[makeQuery(id+"F0.imprint","IMPRINT",EDGE,{"disambiguationData":[TD([[subQ2,-1.0]])],"derivedFrom":subQ1}),1.0]])]});}
            var Q72;
            {var subQ1=sQuery(id+"F0.wireOp",EDGE,"E11");var subQ6=sQuery(id+"F0.wireOp",EDGE,"E12");var subQ9=makeQuery(id+"F0.imprint","INTERSECT",VERTEX,{"disambiguationData":[OD(1.0)],"derivedFrom":[subQ1,subQ6]});Q72=makeQuery(id+"F0.imprint","IMPRINT",FACE,{"disambiguationData":[TD([[makeQuery(id+"F0.imprint","IMPRINT",EDGE,{"disambiguationData":[TD([[subQ9,-1.0]])],"derivedFrom":subQ1}),1.0]])]});}
            var Q73;
            {var subQ0=sQuery(id+"F0.wireOp",EDGE,"E19");var subQ1=sQuery(id+"F0.wireOp",EDGE,"E11");var subQ2=makeQuery(id+"F0.imprint","INTERSECT",VERTEX,{"disambiguationData":[OD(0.0)],"derivedFrom":[subQ1,subQ0]});Q73=makeQuery(id+"F0.imprint","IMPRINT",FACE,{"disambiguationData":[TD([[makeQuery(id+"F0.imprint","IMPRINT",EDGE,{"disambiguationData":[TD([[subQ2,-1.0]])],"derivedFrom":subQ1}),1.0]])]});}
            var Q74;
            {var subQ0=sQuery(id+"F0.wireOp",EDGE,"E26.4");var subQ1=sQuery(id+"F0.wireOp",EDGE,"E11");var subQ2=makeQuery(id+"F0.imprint","INTERSECT",VERTEX,{"derivedFrom":[subQ1,subQ0]});Q74=makeQuery(id+"F0.imprint","IMPRINT",FACE,{"disambiguationData":[TD([[makeQuery(id+"F0.imprint","IMPRINT",EDGE,{"disambiguationData":[TD([[subQ2,-1.0]])],"derivedFrom":subQ1}),-1.0]])]});}
            var Q75;
            {var subQ3=sQuery(id+"F0.wireOp",EDGE,"E26.4");var subQ6=sQuery(id+"F0.wireOp",EDGE,"E11");var subQ9=makeQuery(id+"F0.imprint","INTERSECT",VERTEX,{"derivedFrom":[subQ6,subQ3]});Q75=makeQuery(id+"F0.imprint","IMPRINT",FACE,{"disambiguationData":[TD([[makeQuery(id+"F0.imprint","IMPRINT",EDGE,{"disambiguationData":[TD([[subQ9,-1.0]])],"derivedFrom":subQ6}),1.0]])]});}
            var Q76;
            {var subQ0=sQuery(id+"F0.wireOp",EDGE,"E20.3");var subQ1=sQuery(id+"F0.wireOp",EDGE,"E10");var subQ2=makeQuery(id+"F0.imprint","INTERSECT",VERTEX,{"derivedFrom":[subQ1,subQ0]});Q76=makeQuery(id+"F0.imprint","IMPRINT",FACE,{"disambiguationData":[TD([[makeQuery(id+"F0.imprint","IMPRINT",EDGE,{"disambiguationData":[TD([[subQ2,-1.0]])],"derivedFrom":subQ1}),-1.0]])]});}
            var Q77;
            {var subQ0=sQuery(id+"F0.wireOp",EDGE,"E7");var subQ1=sQuery(id+"F0.wireOp",EDGE,"E6");var subQ2=makeQuery(id+"F0.imprint","INTERSECT",VERTEX,{"derivedFrom":[subQ1,subQ0]});Q77=makeQuery(id+"F0.imprint","IMPRINT",FACE,{"disambiguationData":[TD([[makeQuery(id+"F0.imprint","IMPRINT",EDGE,{"disambiguationData":[TD([[subQ2,-1.0]])],"derivedFrom":subQ1}),1.0]])]});}
            var Q78;
            {var subQ0=sQuery(id+"F0.wireOp",EDGE,"E10");var subQ1=sQuery(id+"F0.wireOp",EDGE,"E7");var subQ2=makeQuery(id+"F0.imprint","INTERSECT",VERTEX,{"disambiguationData":[OD(0.0)],"derivedFrom":[subQ1,subQ0]});Q78=makeQuery(id+"F0.imprint","IMPRINT",FACE,{"disambiguationData":[TD([[makeQuery(id+"F0.imprint","IMPRINT",EDGE,{"disambiguationData":[TD([[subQ2,-1.0]])],"derivedFrom":subQ1}),1.0]])]});}
            var Q79;
            {var subQ1=sQuery(id+"F0.wireOp",EDGE,"E10");var subQ5=sQuery(id+"F0.wireOp",EDGE,"E14.0");var subQ6=makeQuery(id+"F0.imprint","INTERSECT",VERTEX,{"derivedFrom":[subQ1,subQ5]});Q79=makeQuery(id+"F0.imprint","IMPRINT",FACE,{"disambiguationData":[TD([[makeQuery(id+"F0.imprint","IMPRINT",EDGE,{"disambiguationData":[TD([[subQ6,-1.0]])],"derivedFrom":subQ1}),1.0]])]});}
            var Q80;
            {var subQ0=sQuery(id+"F0.wireOp",EDGE,"E14.4");var subQ1=sQuery(id+"F0.wireOp",EDGE,"E10");var subQ2=makeQuery(id+"F0.imprint","INTERSECT",VERTEX,{"derivedFrom":[subQ1,subQ0]});Q80=makeQuery(id+"F0.imprint","IMPRINT",FACE,{"disambiguationData":[TD([[makeQuery(id+"F0.imprint","IMPRINT",EDGE,{"disambiguationData":[TD([[subQ2,-1.0]])],"derivedFrom":subQ1}),1.0]])]});}
            var Q81;
            {var subQ0=sQuery(id+"F0.wireOp",EDGE,"E11");var subQ1=sQuery(id+"F0.wireOp",EDGE,"E10");var subQ2=makeQuery(id+"F0.imprint","INTERSECT",VERTEX,{"disambiguationData":[OD(1.0)],"derivedFrom":[subQ1,subQ0]});Q81=makeQuery(id+"F0.imprint","IMPRINT",FACE,{"disambiguationData":[TD([[makeQuery(id+"F0.imprint","IMPRINT",EDGE,{"disambiguationData":[TD([[subQ2,-1.0]])],"derivedFrom":subQ1}),1.0]])]});}
            var Q82;
            {var subQ0=sQuery(id+"F0.wireOp",EDGE,"E26.4");var subQ1=sQuery(id+"F0.wireOp",EDGE,"E12");var subQ2=makeQuery(id+"F0.imprint","INTERSECT",VERTEX,{"derivedFrom":[subQ1,subQ0]});Q82=makeQuery(id+"F0.imprint","IMPRINT",FACE,{"disambiguationData":[TD([[makeQuery(id+"F0.imprint","IMPRINT",EDGE,{"disambiguationData":[TD([[subQ2,-1.0]])],"derivedFrom":subQ1}),1.0]])]});}
            var Q83;
            {var subQ0=sQuery(id+"F0.wireOp",EDGE,"E12");var subQ1=sQuery(id+"F0.wireOp",EDGE,"E11");var subQ2=makeQuery(id+"F0.imprint","INTERSECT",VERTEX,{"disambiguationData":[OD(1.0)],"derivedFrom":[subQ1,subQ0]});Q83=makeQuery(id+"F0.imprint","IMPRINT",FACE,{"disambiguationData":[TD([[makeQuery(id+"F0.imprint","IMPRINT",EDGE,{"disambiguationData":[TD([[subQ2,-1.0]])],"derivedFrom":subQ1}),-1.0]])]});}
            var Q84;
            {var subQ0=sQuery(id+"F0.wireOp",EDGE,"E19");var subQ1=sQuery(id+"F0.wireOp",EDGE,"E10");var subQ2=makeQuery(id+"F0.imprint","INTERSECT",VERTEX,{"disambiguationData":[OD(1.0)],"derivedFrom":[subQ1,subQ0]});Q84=makeQuery(id+"F0.imprint","IMPRINT",FACE,{"disambiguationData":[TD([[makeQuery(id+"F0.imprint","IMPRINT",EDGE,{"disambiguationData":[TD([[subQ2,-1.0]])],"derivedFrom":subQ1}),1.0]])]});}
            var Q85;
            {var subQ0=sQuery(id+"F0.wireOp",EDGE,"E18");var subQ9=sQuery(id+"F0.wireOp",EDGE,"E9");var subQ10=makeQuery(id+"F0.imprint","INTERSECT",VERTEX,{"disambiguationData":[OD(1.0)],"derivedFrom":[subQ9,subQ0]});Q85=makeQuery(id+"F0.imprint","IMPRINT",FACE,{"disambiguationData":[TD([[makeQuery(id+"F0.imprint","IMPRINT",EDGE,{"disambiguationData":[TD([[subQ10,-1.0]])],"derivedFrom":subQ9}),1.0]])]});}
            var Q86;
            {var subQ0=sQuery(id+"F0.wireOp",EDGE,"E19");var subQ1=sQuery(id+"F0.wireOp",EDGE,"E10");var subQ2=makeQuery(id+"F0.imprint","INTERSECT",VERTEX,{"disambiguationData":[OD(0.0)],"derivedFrom":[subQ1,subQ0]});Q86=makeQuery(id+"F0.imprint","IMPRINT",FACE,{"disambiguationData":[TD([[makeQuery(id+"F0.imprint","IMPRINT",EDGE,{"disambiguationData":[TD([[subQ2,-1.0]])],"derivedFrom":subQ1}),1.0]])]});}
            var Q87;
            {var subQ1=sQuery(id+"F0.wireOp",EDGE,"E10");var subQ7=sQuery(id+"F0.wireOp",EDGE,"E26.0");var subQ9=makeQuery(id+"F0.imprint","INTERSECT",VERTEX,{"derivedFrom":[subQ1,subQ7]});Q87=makeQuery(id+"F0.imprint","IMPRINT",FACE,{"disambiguationData":[TD([[makeQuery(id+"F0.imprint","IMPRINT",EDGE,{"disambiguationData":[TD([[subQ9,-1.0]])],"derivedFrom":subQ1}),1.0]])]});}
            var Q88;
            {var subQ0=sQuery(id+"F0.wireOp",EDGE,"E26.0");var subQ1=sQuery(id+"F0.wireOp",EDGE,"E10");var subQ2=makeQuery(id+"F0.imprint","INTERSECT",VERTEX,{"derivedFrom":[subQ1,subQ0]});Q88=makeQuery(id+"F0.imprint","IMPRINT",FACE,{"disambiguationData":[TD([[makeQuery(id+"F0.imprint","IMPRINT",EDGE,{"disambiguationData":[TD([[subQ2,-1.0]])],"derivedFrom":subQ1}),-1.0]])]});}
            var Q89;
            {var subQ0=sQuery(id+"F0.wireOp",EDGE,"E18");var subQ1=sQuery(id+"F0.wireOp",EDGE,"E10");var subQ2=makeQuery(id+"F0.imprint","INTERSECT",VERTEX,{"disambiguationData":[OD(1.0)],"derivedFrom":[subQ1,subQ0]});Q89=makeQuery(id+"F0.imprint","IMPRINT",FACE,{"disambiguationData":[TD([[makeQuery(id+"F0.imprint","IMPRINT",EDGE,{"disambiguationData":[TD([[subQ2,-1.0]])],"derivedFrom":subQ1}),1.0]])]});}
            var Q90;
            {var subQ0=sQuery(id+"F0.wireOp",EDGE,"E26.4");var subQ1=sQuery(id+"F0.wireOp",EDGE,"E10");var subQ2=makeQuery(id+"F0.imprint","INTERSECT",VERTEX,{"derivedFrom":[subQ1,subQ0]});Q90=makeQuery(id+"F0.imprint","IMPRINT",FACE,{"disambiguationData":[TD([[makeQuery(id+"F0.imprint","IMPRINT",EDGE,{"disambiguationData":[TD([[subQ2,-1.0]])],"derivedFrom":subQ1}),1.0]])]});}
            var Q91;
            {var subQ3=sQuery(id+"F0.wireOp",EDGE,"E20.4");var subQ7=sQuery(id+"F0.wireOp",EDGE,"E9");var subQ9=makeQuery(id+"F0.imprint","INTERSECT",VERTEX,{"derivedFrom":[subQ7,subQ3]});Q91=makeQuery(id+"F0.imprint","IMPRINT",FACE,{"disambiguationData":[TD([[makeQuery(id+"F0.imprint","IMPRINT",EDGE,{"disambiguationData":[TD([[subQ9,-1.0]])],"derivedFrom":subQ7}),1.0]])]});}
            var Q92;
            {var subQ0=sQuery(id+"F0.wireOp",EDGE,"E13");var subQ1=sQuery(id+"F0.wireOp",EDGE,"E11");var subQ2=makeQuery(id+"F0.imprint","INTERSECT",VERTEX,{"disambiguationData":[OD(1.0)],"derivedFrom":[subQ1,subQ0]});Q92=makeQuery(id+"F0.imprint","IMPRINT",FACE,{"disambiguationData":[TD([[makeQuery(id+"F0.imprint","IMPRINT",EDGE,{"disambiguationData":[TD([[subQ2,-1.0]])],"derivedFrom":subQ1}),-1.0]])]});}
            var Q93;
            {var subQ0=sQuery(id+"F0.wireOp",EDGE,"E13");var subQ1=sQuery(id+"F0.wireOp",EDGE,"E9");var subQ2=makeQuery(id+"F0.imprint","INTERSECT",VERTEX,{"disambiguationData":[OD(1.0)],"derivedFrom":[subQ1,subQ0]});Q93=makeQuery(id+"F0.imprint","IMPRINT",FACE,{"disambiguationData":[TD([[makeQuery(id+"F0.imprint","IMPRINT",EDGE,{"disambiguationData":[TD([[subQ2,-1.0]])],"derivedFrom":subQ1}),1.0]])]});}
            var Q94;
            {var subQ0=sQuery(id+"F0.wireOp",EDGE,"E20.4");var subQ1=sQuery(id+"F0.wireOp",EDGE,"E9");var subQ2=makeQuery(id+"F0.imprint","INTERSECT",VERTEX,{"derivedFrom":[subQ1,subQ0]});Q94=makeQuery(id+"F0.imprint","IMPRINT",FACE,{"disambiguationData":[TD([[makeQuery(id+"F0.imprint","IMPRINT",EDGE,{"disambiguationData":[TD([[subQ2,-1.0]])],"derivedFrom":subQ1}),-1.0]])]});}
            var Q95;
            {var subQ5=sQuery(id+"F0.wireOp",EDGE,"E8");var subQ6=sQuery(id+"F0.wireOp",EDGE,"E4");var subQ7=makeQuery(id+"F0.imprint","INTERSECT",VERTEX,{"derivedFrom":[subQ6,subQ5]});Q95=makeQuery(id+"F0.imprint","IMPRINT",FACE,{"disambiguationData":[TD([[makeQuery(id+"F0.imprint","IMPRINT",EDGE,{"disambiguationData":[TD([[subQ7,1.0]])],"derivedFrom":subQ5}),1.0]])]});}
            var Q96;
            {var subQ0=sQuery(id+"F0.wireOp",EDGE,"E10");var subQ1=sQuery(id+"F0.wireOp",EDGE,"E9");var subQ2=makeQuery(id+"F0.imprint","INTERSECT",VERTEX,{"disambiguationData":[OD(1.0)],"derivedFrom":[subQ1,subQ0]});Q96=makeQuery(id+"F0.imprint","IMPRINT",FACE,{"disambiguationData":[TD([[makeQuery(id+"F0.imprint","IMPRINT",EDGE,{"disambiguationData":[TD([[subQ2,-1.0]])],"derivedFrom":subQ1}),1.0]])]});}
            var Q97;
            {var subQ0=sQuery(id+"F0.wireOp",EDGE,"E14.0");var subQ1=sQuery(id+"F0.wireOp",EDGE,"E9");var subQ2=makeQuery(id+"F0.imprint","INTERSECT",VERTEX,{"derivedFrom":[subQ1,subQ0]});Q97=makeQuery(id+"F0.imprint","IMPRINT",FACE,{"disambiguationData":[TD([[makeQuery(id+"F0.imprint","IMPRINT",EDGE,{"disambiguationData":[TD([[subQ2,-1.0]])],"derivedFrom":subQ1}),1.0]])]});}
            var Q98;
            {var subQ0=sQuery(id+"F0.wireOp",EDGE,"E14.1");var subQ1=sQuery(id+"F0.wireOp",EDGE,"E9");var subQ2=makeQuery(id+"F0.imprint","INTERSECT",VERTEX,{"derivedFrom":[subQ1,subQ0]});Q98=makeQuery(id+"F0.imprint","IMPRINT",FACE,{"disambiguationData":[TD([[makeQuery(id+"F0.imprint","IMPRINT",EDGE,{"disambiguationData":[TD([[subQ2,-1.0]])],"derivedFrom":subQ1}),1.0]])]});}
            var Q99;
            {var subQ0=sQuery(id+"F0.wireOp",EDGE,"E18");var subQ1=sQuery(id+"F0.wireOp",EDGE,"E9");var subQ2=makeQuery(id+"F0.imprint","INTERSECT",VERTEX,{"disambiguationData":[OD(0.0)],"derivedFrom":[subQ1,subQ0]});Q99=makeQuery(id+"F0.imprint","IMPRINT",FACE,{"disambiguationData":[TD([[makeQuery(id+"F0.imprint","IMPRINT",EDGE,{"disambiguationData":[TD([[subQ2,-1.0]])],"derivedFrom":subQ1}),1.0]])]});}
            var Q100;
            {var subQ3=sQuery(id+"F0.wireOp",EDGE,"E20.0");var subQ6=sQuery(id+"F0.wireOp",EDGE,"E8");var subQ9=makeQuery(id+"F0.imprint","INTERSECT",VERTEX,{"derivedFrom":[subQ6,subQ3]});Q100=makeQuery(id+"F0.imprint","IMPRINT",FACE,{"disambiguationData":[TD([[makeQuery(id+"F0.imprint","IMPRINT",EDGE,{"disambiguationData":[TD([[subQ9,-1.0]])],"derivedFrom":subQ6}),1.0]])]});}
            var Q101;
            {var subQ0=sQuery(id+"F0.wireOp",EDGE,"E13");var subQ1=sQuery(id+"F0.wireOp",EDGE,"E8");var subQ2=makeQuery(id+"F0.imprint","INTERSECT",VERTEX,{"disambiguationData":[OD(1.0)],"derivedFrom":[subQ1,subQ0]});Q101=makeQuery(id+"F0.imprint","IMPRINT",FACE,{"disambiguationData":[TD([[makeQuery(id+"F0.imprint","IMPRINT",EDGE,{"disambiguationData":[TD([[subQ2,-1.0]])],"derivedFrom":subQ1}),1.0]])]});}
            var Q102;
            {var subQ0=sQuery(id+"F0.wireOp",EDGE,"E10");var subQ1=sQuery(id+"F0.wireOp",EDGE,"E4");var subQ2=makeQuery(id+"F0.imprint","INTERSECT",VERTEX,{"derivedFrom":[subQ1,subQ0]});Q102=makeQuery(id+"F0.imprint","IMPRINT",FACE,{"disambiguationData":[TD([[makeQuery(id+"F0.imprint","IMPRINT",EDGE,{"disambiguationData":[TD([[subQ2,-1.0]])],"derivedFrom":subQ1}),1.0]])]});}
            var Q103;
            {var subQ0=sQuery(id+"F0.wireOp",EDGE,"E17");var subQ1=sQuery(id+"F0.wireOp",EDGE,"E8");var subQ2=makeQuery(id+"F0.imprint","INTERSECT",VERTEX,{"disambiguationData":[OD(1.0)],"derivedFrom":[subQ1,subQ0]});Q103=makeQuery(id+"F0.imprint","IMPRINT",FACE,{"disambiguationData":[TD([[makeQuery(id+"F0.imprint","IMPRINT",EDGE,{"disambiguationData":[TD([[subQ2,-1.0]])],"derivedFrom":subQ1}),1.0]])]});}
            var Q104;
            {var subQ0=sQuery(id+"F0.wireOp",EDGE,"E13");var subQ1=sQuery(id+"F0.wireOp",EDGE,"E10");var subQ2=makeQuery(id+"F0.imprint","INTERSECT",VERTEX,{"disambiguationData":[OD(0.0)],"derivedFrom":[subQ1,subQ0]});Q104=makeQuery(id+"F0.imprint","IMPRINT",FACE,{"disambiguationData":[TD([[makeQuery(id+"F0.imprint","IMPRINT",EDGE,{"disambiguationData":[TD([[subQ2,-1.0]])],"derivedFrom":subQ1}),-1.0]])]});}
            var Q105;
            {var subQ0=sQuery(id+"F0.wireOp",EDGE,"E26.0");var subQ1=sQuery(id+"F0.wireOp",EDGE,"E9");var subQ2=makeQuery(id+"F0.imprint","INTERSECT",VERTEX,{"derivedFrom":[subQ1,subQ0]});Q105=makeQuery(id+"F0.imprint","IMPRINT",FACE,{"disambiguationData":[TD([[makeQuery(id+"F0.imprint","IMPRINT",EDGE,{"disambiguationData":[TD([[subQ2,-1.0]])],"derivedFrom":subQ1}),1.0]])]});}
            var Q106;
            {var subQ0=sQuery(id+"F0.wireOp",EDGE,"E26.1");var subQ1=sQuery(id+"F0.wireOp",EDGE,"E9");var subQ2=makeQuery(id+"F0.imprint","INTERSECT",VERTEX,{"derivedFrom":[subQ1,subQ0]});Q106=makeQuery(id+"F0.imprint","IMPRINT",FACE,{"disambiguationData":[TD([[makeQuery(id+"F0.imprint","IMPRINT",EDGE,{"disambiguationData":[TD([[subQ2,-1.0]])],"derivedFrom":subQ1}),-1.0]])]});}
            var Q107;
            {var subQ1=sQuery(id+"F0.wireOp",EDGE,"E9");var subQ7=sQuery(id+"F0.wireOp",EDGE,"E26.1");var subQ9=makeQuery(id+"F0.imprint","INTERSECT",VERTEX,{"derivedFrom":[subQ1,subQ7]});Q107=makeQuery(id+"F0.imprint","IMPRINT",FACE,{"disambiguationData":[TD([[makeQuery(id+"F0.imprint","IMPRINT",EDGE,{"disambiguationData":[TD([[subQ9,-1.0]])],"derivedFrom":subQ1}),1.0]])]});}
            var Q108;
            {var subQ0=sQuery(id+"F0.wireOp",EDGE,"E20.0");var subQ1=sQuery(id+"F0.wireOp",EDGE,"E8");var subQ2=makeQuery(id+"F0.imprint","INTERSECT",VERTEX,{"derivedFrom":[subQ1,subQ0]});Q108=makeQuery(id+"F0.imprint","IMPRINT",FACE,{"disambiguationData":[TD([[makeQuery(id+"F0.imprint","IMPRINT",EDGE,{"disambiguationData":[TD([[subQ2,-1.0]])],"derivedFrom":subQ1}),-1.0]])]});}
            var Q109;
            {var subQ1=sQuery(id+"F0.wireOp",EDGE,"E8");var subQ5=sQuery(id+"F0.wireOp",EDGE,"E14.2");var subQ9=makeQuery(id+"F0.imprint","INTERSECT",VERTEX,{"derivedFrom":[subQ1,subQ5]});Q109=makeQuery(id+"F0.imprint","IMPRINT",FACE,{"disambiguationData":[TD([[makeQuery(id+"F0.imprint","IMPRINT",EDGE,{"disambiguationData":[TD([[subQ9,-1.0]])],"derivedFrom":subQ1}),1.0]])]});}
            var Q110;
            {var subQ5=sQuery(id+"F0.wireOp",EDGE,"E8");var subQ7=sQuery(id+"F0.wireOp",EDGE,"E14.1");var subQ8=makeQuery(id+"F0.imprint","INTERSECT",VERTEX,{"derivedFrom":[subQ5,subQ7]});Q110=makeQuery(id+"F0.imprint","IMPRINT",FACE,{"disambiguationData":[TD([[makeQuery(id+"F0.imprint","IMPRINT",EDGE,{"disambiguationData":[TD([[subQ8,-1.0]])],"derivedFrom":subQ5}),1.0]])]});}
            var Q111;
            {var subQ0=sQuery(id+"F0.wireOp",EDGE,"E9");var subQ1=sQuery(id+"F0.wireOp",EDGE,"E8");var subQ2=makeQuery(id+"F0.imprint","INTERSECT",VERTEX,{"disambiguationData":[OD(1.0)],"derivedFrom":[subQ1,subQ0]});Q111=makeQuery(id+"F0.imprint","IMPRINT",FACE,{"disambiguationData":[TD([[makeQuery(id+"F0.imprint","IMPRINT",EDGE,{"disambiguationData":[TD([[subQ2,-1.0]])],"derivedFrom":subQ1}),1.0]])]});}
            var Q112;
            {var subQ0=sQuery(id+"F0.wireOp",EDGE,"E17");var subQ1=sQuery(id+"F0.wireOp",EDGE,"E9");var subQ2=makeQuery(id+"F0.imprint","INTERSECT",VERTEX,{"disambiguationData":[OD(1.0)],"derivedFrom":[subQ1,subQ0]});Q112=makeQuery(id+"F0.imprint","IMPRINT",FACE,{"disambiguationData":[TD([[makeQuery(id+"F0.imprint","IMPRINT",EDGE,{"disambiguationData":[TD([[subQ2,-1.0]])],"derivedFrom":subQ1}),1.0]])]});}
            var Q113;
            {var subQ1=sQuery(id+"F0.wireOp",EDGE,"E8");var subQ7=sQuery(id+"F0.wireOp",EDGE,"E26.2");var subQ9=makeQuery(id+"F0.imprint","INTERSECT",VERTEX,{"derivedFrom":[subQ1,subQ7]});Q113=makeQuery(id+"F0.imprint","IMPRINT",FACE,{"disambiguationData":[TD([[makeQuery(id+"F0.imprint","IMPRINT",EDGE,{"disambiguationData":[TD([[subQ9,-1.0]])],"derivedFrom":subQ1}),1.0]])]});}
            var Q114;
            {var subQ0=sQuery(id+"F0.wireOp",EDGE,"E16");var subQ1=sQuery(id+"F0.wireOp",EDGE,"E8");var subQ2=makeQuery(id+"F0.imprint","INTERSECT",VERTEX,{"disambiguationData":[OD(1.0)],"derivedFrom":[subQ1,subQ0]});Q114=makeQuery(id+"F0.imprint","IMPRINT",FACE,{"disambiguationData":[TD([[makeQuery(id+"F0.imprint","IMPRINT",EDGE,{"disambiguationData":[TD([[subQ2,-1.0]])],"derivedFrom":subQ1}),1.0]])]});}
            var Q115;
            {var subQ0=sQuery(id+"F0.wireOp",EDGE,"E17");var subQ1=sQuery(id+"F0.wireOp",EDGE,"E8");var subQ2=makeQuery(id+"F0.imprint","INTERSECT",VERTEX,{"disambiguationData":[OD(0.0)],"derivedFrom":[subQ1,subQ0]});Q115=makeQuery(id+"F0.imprint","IMPRINT",FACE,{"disambiguationData":[TD([[makeQuery(id+"F0.imprint","IMPRINT",EDGE,{"disambiguationData":[TD([[subQ2,-1.0]])],"derivedFrom":subQ1}),1.0]])]});}
            var Q116;
            {var subQ0=sQuery(id+"F0.wireOp",EDGE,"E14.2");var subQ1=sQuery(id+"F0.wireOp",EDGE,"E12");var subQ2=makeQuery(id+"F0.imprint","INTERSECT",VERTEX,{"derivedFrom":[subQ1,subQ0]});Q116=makeQuery(id+"F0.imprint","IMPRINT",FACE,{"disambiguationData":[TD([[makeQuery(id+"F0.imprint","IMPRINT",EDGE,{"disambiguationData":[TD([[subQ2,-1.0]])],"derivedFrom":subQ1}),1.0]])]});}
            var Q117;
            {var subQ0=sQuery(id+"F0.wireOp",EDGE,"E26.2");var subQ1=sQuery(id+"F0.wireOp",EDGE,"E8");var subQ2=makeQuery(id+"F0.imprint","INTERSECT",VERTEX,{"derivedFrom":[subQ1,subQ0]});Q117=makeQuery(id+"F0.imprint","IMPRINT",FACE,{"disambiguationData":[TD([[makeQuery(id+"F0.imprint","IMPRINT",EDGE,{"disambiguationData":[TD([[subQ2,-1.0]])],"derivedFrom":subQ1}),-1.0]])]});}
            var Q118;
            {var subQ0=sQuery(id+"F0.wireOp",EDGE,"E26.1");var subQ1=sQuery(id+"F0.wireOp",EDGE,"E8");var subQ2=makeQuery(id+"F0.imprint","INTERSECT",VERTEX,{"derivedFrom":[subQ1,subQ0]});Q118=makeQuery(id+"F0.imprint","IMPRINT",FACE,{"disambiguationData":[TD([[makeQuery(id+"F0.imprint","IMPRINT",EDGE,{"disambiguationData":[TD([[subQ2,-1.0]])],"derivedFrom":subQ1}),1.0]])]});}
            var Q119;
            {var subQ1=sQuery(id+"F0.wireOp",EDGE,"E7");var subQ7=sQuery(id+"F0.wireOp",EDGE,"E20.1");var subQ8=makeQuery(id+"F0.imprint","INTERSECT",VERTEX,{"derivedFrom":[subQ1,subQ7]});Q119=makeQuery(id+"F0.imprint","IMPRINT",FACE,{"disambiguationData":[TD([[makeQuery(id+"F0.imprint","IMPRINT",EDGE,{"disambiguationData":[TD([[subQ8,-1.0]])],"derivedFrom":subQ1}),1.0]])]});}
            var Q120;
            {var subQ0=sQuery(id+"F0.wireOp",EDGE,"E13");var subQ1=sQuery(id+"F0.wireOp",EDGE,"E12");var subQ2=makeQuery(id+"F0.imprint","INTERSECT",VERTEX,{"disambiguationData":[OD(0.0)],"derivedFrom":[subQ1,subQ0]});Q120=makeQuery(id+"F0.imprint","IMPRINT",FACE,{"disambiguationData":[TD([[makeQuery(id+"F0.imprint","IMPRINT",EDGE,{"disambiguationData":[TD([[subQ2,-1.0]])],"derivedFrom":subQ1}),-1.0]])]});}
            var Q121;
            {var subQ0=sQuery(id+"F0.wireOp",EDGE,"E12");var subQ1=sQuery(id+"F0.wireOp",EDGE,"E8");var subQ2=makeQuery(id+"F0.imprint","INTERSECT",VERTEX,{"disambiguationData":[OD(1.0)],"derivedFrom":[subQ1,subQ0]});Q121=makeQuery(id+"F0.imprint","IMPRINT",FACE,{"disambiguationData":[TD([[makeQuery(id+"F0.imprint","IMPRINT",EDGE,{"disambiguationData":[TD([[subQ2,-1.0]])],"derivedFrom":subQ1}),1.0]])]});}
            var Q122;
            {var subQ0=sQuery(id+"F0.wireOp",EDGE,"E26.3");var subQ1=sQuery(id+"F0.wireOp",EDGE,"E11");var subQ2=makeQuery(id+"F0.imprint","INTERSECT",VERTEX,{"derivedFrom":[subQ1,subQ0]});Q122=makeQuery(id+"F0.imprint","IMPRINT",FACE,{"disambiguationData":[TD([[makeQuery(id+"F0.imprint","IMPRINT",EDGE,{"disambiguationData":[TD([[subQ2,-1.0]])],"derivedFrom":subQ1}),1.0]])]});}
            extrude(context, id + "F1", {"entities" : qUnion([Q0, Q1, Q2, Q3, Q4, Q5, Q6, Q7, Q8, Q9, Q10, Q11, Q12, Q13, Q14, Q15, Q16, Q17, Q18, Q19, Q20, Q21, Q22, Q23, Q24, Q25, Q26, Q27, Q28, Q29, Q30, Q31, Q32, Q33, Q34, Q35, Q36, Q37, Q38, Q39, Q40, Q41, Q42, Q43, Q44, Q45, Q46, Q47, Q48, Q49, Q50, Q51, Q52, Q53, Q54, Q55, Q56, Q57, Q58, Q59, Q60, Q61, Q62, Q63, Q64, Q65, Q66, Q67, Q68, Q69, Q70, Q71, Q72, Q73, Q74, Q75, Q76, Q77, Q78, Q79, Q80, Q81, Q82, Q83, Q84, Q85, Q86, Q87, Q88, Q89, Q90, Q91, Q92, Q93, Q94, Q95, Q96, Q97, Q98, Q99, Q100, Q101, Q102, Q103, Q104, Q105, Q106, Q107, Q108, Q109, Q110, Q111, Q112, Q113, Q114, Q115, Q116, Q117, Q118, Q119, Q120, Q121, Q122]), "flatOperationType" : FlatOperationType.REMOVE, "depth" : 6.35 * mm, "offsetDistance" : 25.4 * mm, "domain" : OperationDomain.MODEL});
        }
    });
